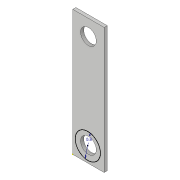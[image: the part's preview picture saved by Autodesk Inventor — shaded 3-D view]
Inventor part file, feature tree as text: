
AUTODESK INVENTOR PART (.ipt)
format: ipt  version: 2019 (Build 230136000, 136)  size: 92,160 bytes
history: native  units: in
note: dims shown in document units (in); Inventor stores cm internally (conversion verified against a paired STEP export)
features: sketch x3, extrude x2
ambient origin geometry x8: Origin, YZ Plane, XZ Plane, XY Plane, X Axis, Y Axis, Z Axis, Center Point
bodies: Solid1 (feature_tree)
feature tree (5):
  extrude  "Extrusion1"  Depth=1.5748in
  extrude  "Extrusion2"  Depth=0.0394in
  sketch  "Sketch3"  dims[d5=0.1969in d6=0.1969in d7=0.0394in d8=0.1575in d9=0.1969in d10=0.1969in d11=0.0394in d12=0.0in d13=0.315in]
  sketch  "Sketch1"  dims[d0=0.3937in d1=1.5748in]
  sketch  "Sketch2"  dims[d2=0.0394in d3=0.0in d4=0.1969in]
